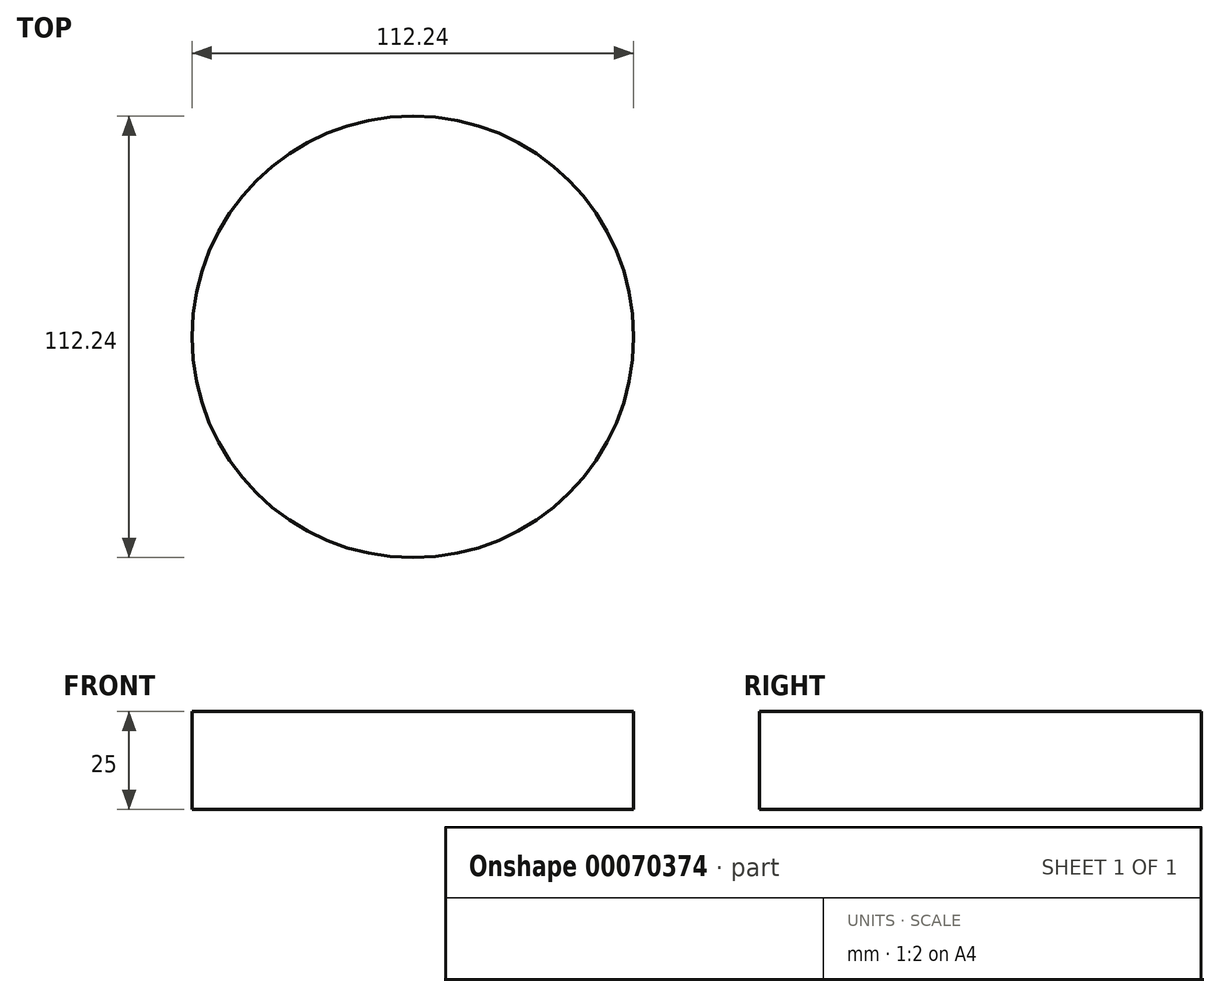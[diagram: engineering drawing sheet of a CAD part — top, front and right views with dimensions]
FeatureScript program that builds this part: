
annotation { "Feature Type Name" : "Feature", "Feature Type Description" : "" }
export const myFeature = defineFeature(function(context is Context, id is Id, definition is map)
    precondition{}
    {
        {
            var Q0;
            Q0=qCreatedBy(makeId("Top.planeOp"),FACE);
            var sketch = newSketch(context, id + "F0", { "sketchPlane" : qUnion([Q0])});
            skCircle(sketch, "E0", {"center": v(0, 0) * mm, "radius": 56.12 * mm});
            skSolve(sketch);
        }
        {
            var Q0;
            Q0=makeQuery(id+"F0.imprint","IMPRINT",FACE,{"disambiguationData":[TD([[makeQuery(id+"F0.imprint","IMPRINT",EDGE,{"derivedFrom":sQuery(id+"F0.wireOp",EDGE,"E0")}),1.0]])]});
            extrude(context, id + "F1", {"entities" : qUnion([Q0]), "depth" : 25 * mm, "offsetDistance" : 25 * mm});
        }
    });
